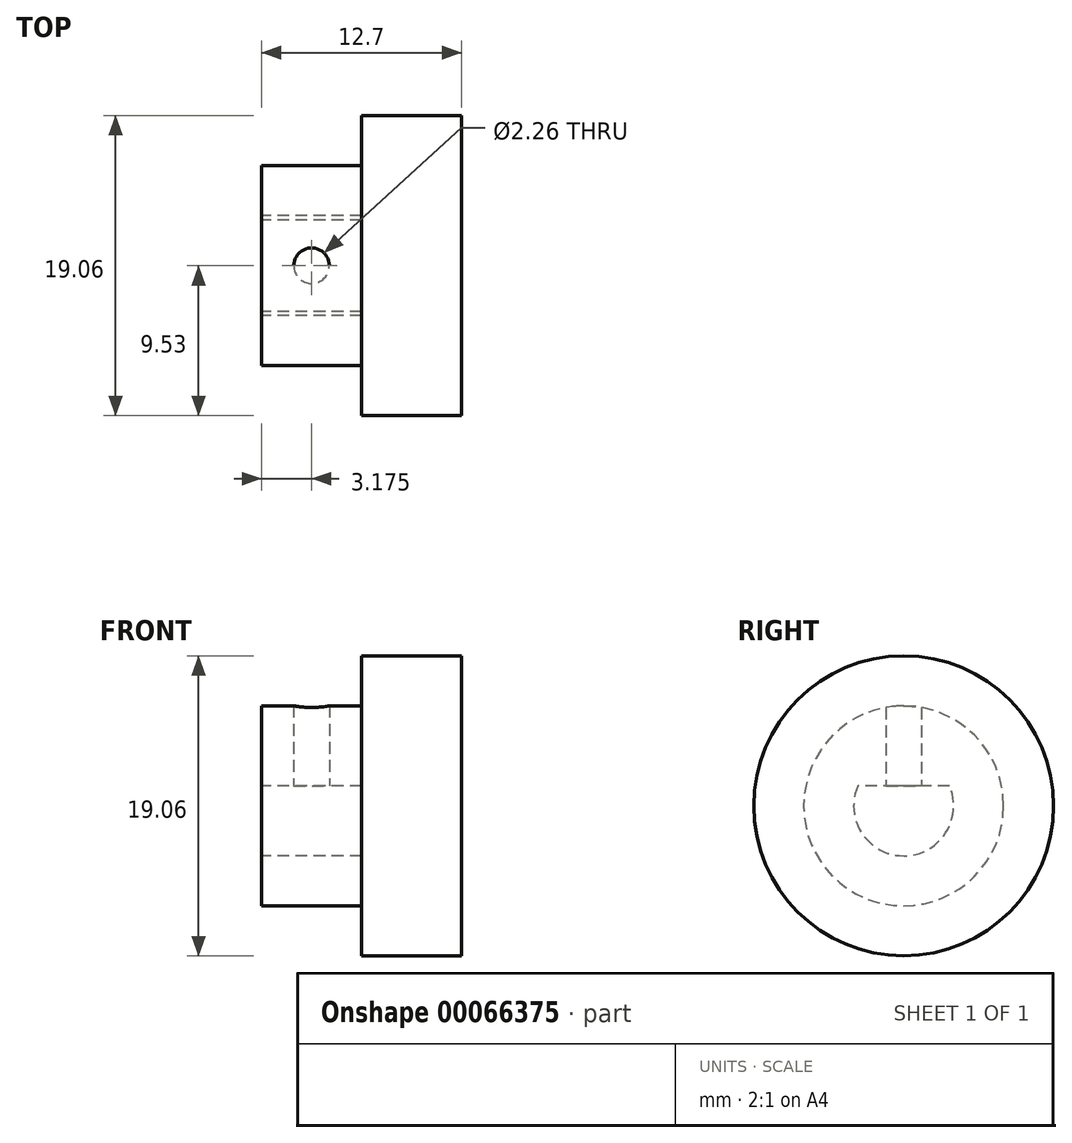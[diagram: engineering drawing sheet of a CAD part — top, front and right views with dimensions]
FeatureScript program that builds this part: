
annotation { "Feature Type Name" : "Feature", "Feature Type Description" : "" }
export const myFeature = defineFeature(function(context is Context, id is Id, definition is map)
    precondition{}
    {
        {
            var Q0;
            Q0=qCreatedBy(makeId("Right.planeOp"),FACE);
            var sketch = newSketch(context, id + "F0", { "sketchPlane" : qUnion([Q0])});
            skCircle(sketch, "E0", {"center": v(0, 0) * mm, "radius": 9.53 * mm});
            skSolve(sketch);
        }
        {
            var Q0;
            Q0 = qSketchRegion(id + "F0", true);
            extrude(context, id + "F1", {"entities" : qUnion([Q0]), "depth" : 12.7 * mm});
        }
        {
            var Q0;
            Q0=makeQuery(id+"F1.opExtrude","CAP_FACE",FACE,{"disambiguationData":[OSD([sQuery(id+"F0.wireOp",EDGE,"E0")])],"isStart":true});
            var sketch = newSketch(context, id + "F2", { "sketchPlane" : qUnion([Q0])});
            skCircle(sketch, "E1", {"center": v(0, 0) * mm, "radius": 6.35 * mm});
            skCircle(sketch, "E2", {"center": v(0, 0) * mm, "radius": 9.53 * mm});
            skSolve(sketch);
        }
        {
            var Q0;
            Q0 = qSketchRegion(id + "F2", true);
            extrude(context, id + "F3", {"entities" : qUnion([Q0]), "operationType" : NewBodyOperationType.REMOVE, "oppositeDirection" : true, "depth" : 6.35 * mm});
        }
        {
            var Q0;
            Q0=makeQuery(id+"F1.opExtrude","CAP_FACE",FACE,{"disambiguationData":[OSD([sQuery(id+"F0.wireOp",EDGE,"E0")])],"isStart":true});
            var sketch = newSketch(context, id + "F4", { "sketchPlane" : qUnion([Q0])});
            skArc(sketch, "E3", {"start": v(-2.9, 1.27) * mm, "mid": v(0, -3.18) * mm, "end": v(2.9, 1.27) * mm});
            skLineSegment(sketch, "E4", {"start": v(-2.9, 1.27) * mm, "end": v(2.9, 1.27) * mm});
            skSolve(sketch);
        }
        {
            var Q0;
            Q0 = qSketchRegion(id + "F4", true);
            extrude(context, id + "F5", {"entities" : qUnion([Q0]), "operationType" : NewBodyOperationType.REMOVE, "oppositeDirection" : true, "depth" : 6.35 * mm});
        }
        {
            var Q0;
            Q0=makeQuery(id+"F5.boolean.opBoolean","COPY",FACE,{"derivedFrom":makeQuery(id+"F5.opExtrude","SWEPT_FACE",FACE,{"disambiguationData":[OSD([sQuery(id+"F4.wireOp",EDGE,"E4")])]})});
            var sketch = newSketch(context, id + "F6", { "sketchPlane" : qUnion([Q0])});
            skLineSegment(sketch, "E5", {"start": v(3.18, -2.9) * mm, "end": v(3.18, 2.9) * mm, "construction": true});
            skPoint(sketch, "E6", {"position": v(3.18, 0) * mm});
            skSolve(sketch);
        }
        {
            var Q0;
            Q0=sQuery(id+"F6.wireOp",VERTEX,"E6");
            var Q1;
            Q1=makeQuery(id+"F1.opExtrude","SWEPT_BODY",BODY,{"disambiguationData":[OSD([sQuery(id+"F0.wireOp",EDGE,"E0")])]});
            hole(context, id + "F7", {"style" : HoleStyle.SIMPLE, "holeDiameter" : 2.26 * mm, "endStyle" : HoleEndStyle.THROUGH, "locations" : qUnion([Q0]), "scope" : qUnion([Q1])});
        }
    });
